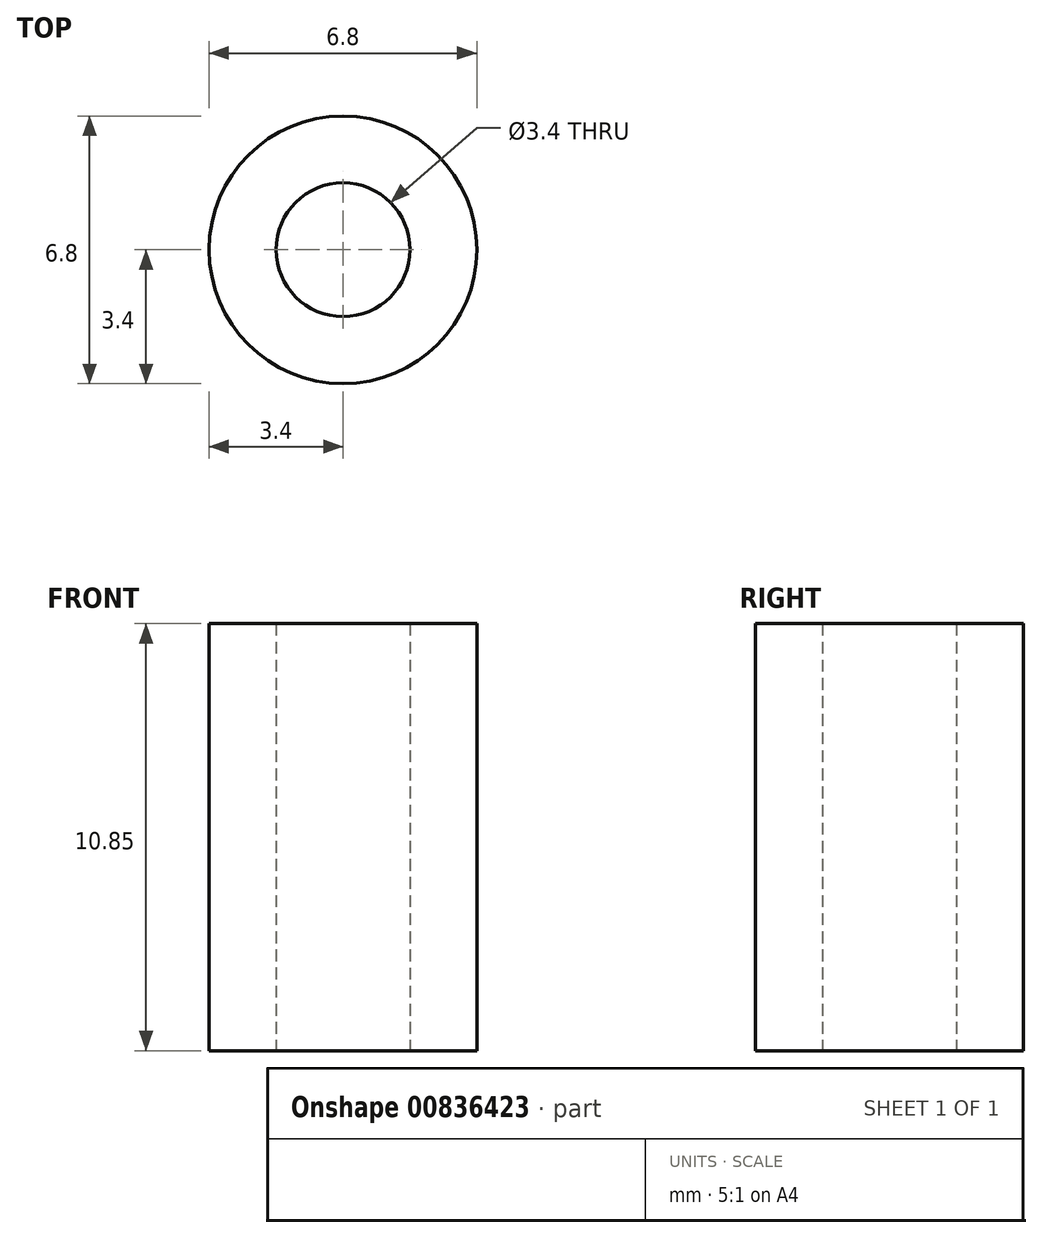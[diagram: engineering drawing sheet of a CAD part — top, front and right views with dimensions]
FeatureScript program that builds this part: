
annotation { "Feature Type Name" : "Feature", "Feature Type Description" : "" }
export const myFeature = defineFeature(function(context is Context, id is Id, definition is map)
    precondition{}
    {
        {
            var Q0;
            Q0=qCreatedBy(makeId("Top.planeOp"),FACE);
            var sketch = newSketch(context, id + "F0", { "sketchPlane" : qUnion([Q0])});
            skCircle(sketch, "E0", {"center": v(0, 0) * mm, "radius": 3.4 * mm});
            skCircle(sketch, "E1", {"center": v(0, 0) * mm, "radius": 1.7 * mm});
            skSolve(sketch);
        }
        {
            var Q0;
            Q0=makeQuery(id+"F0.imprint","IMPRINT",FACE,{"disambiguationData":[TD([[makeQuery(id+"F0.imprint","IMPRINT",EDGE,{"derivedFrom":sQuery(id+"F0.wireOp",EDGE,"E0")}),1.0]])]});
            extrude(context, id + "F1", {"entities" : qUnion([Q0]), "depth" : 10.85 * mm, "offsetDistance" : 25 * mm});
        }
    });
